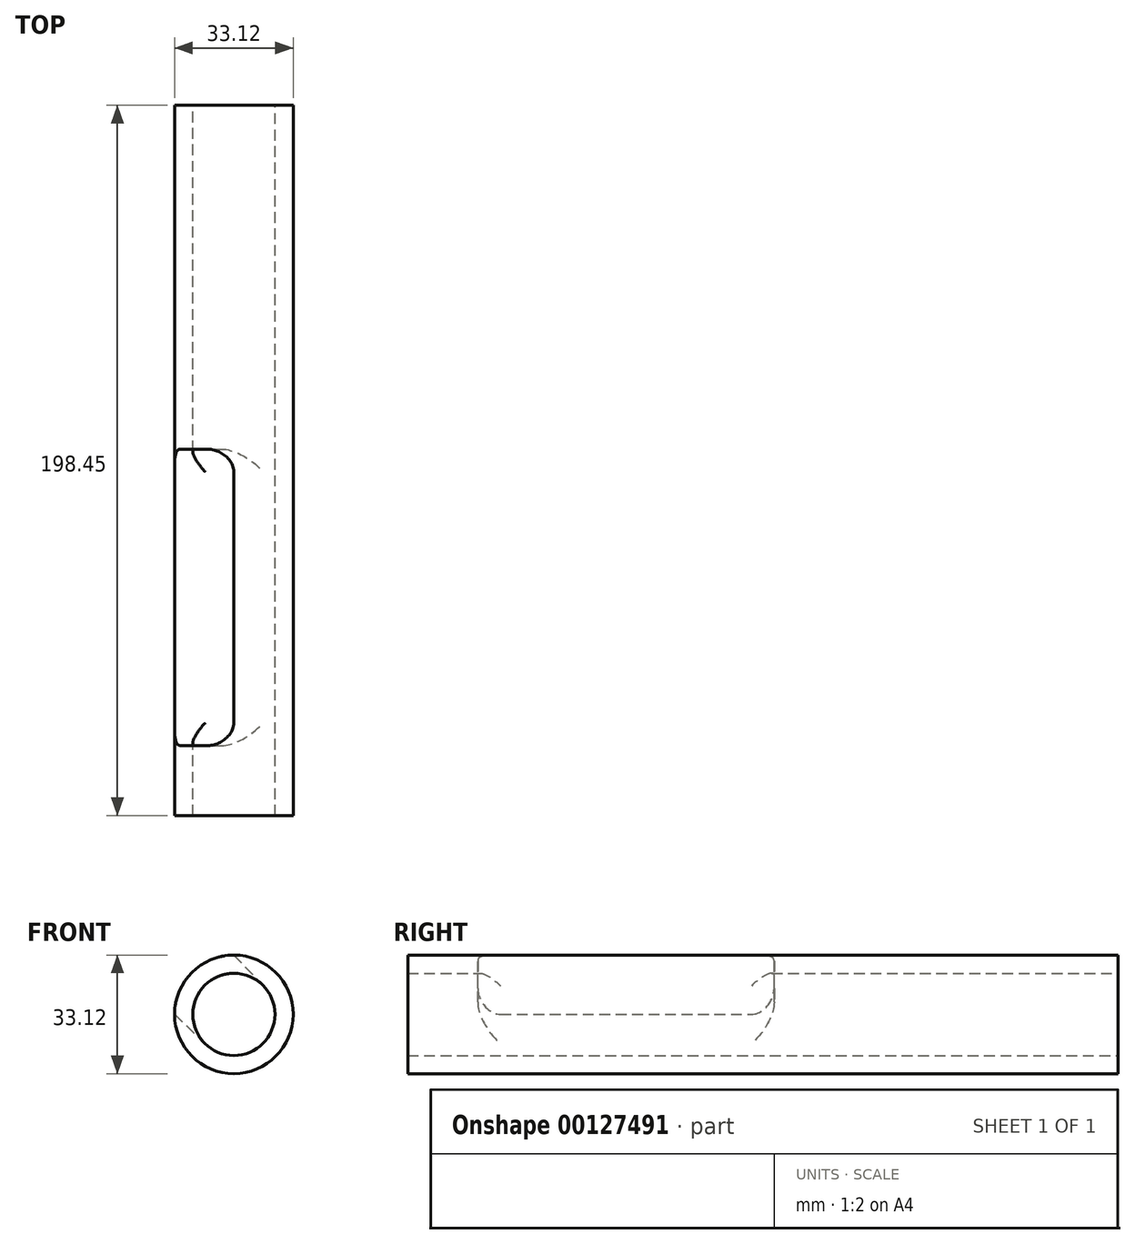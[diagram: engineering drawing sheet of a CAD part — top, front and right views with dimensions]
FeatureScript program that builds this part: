
annotation { "Feature Type Name" : "Feature", "Feature Type Description" : "" }
export const myFeature = defineFeature(function(context is Context, id is Id, definition is map)
    precondition{}
    {
        {
            var Q0;
            Q0=qCreatedBy(makeId("Front.planeOp"),FACE);
            var sketch = newSketch(context, id + "F0", { "sketchPlane" : qUnion([Q0])});
            skCircle(sketch, "E0", {"center": v(0, 0) * mm, "radius": 16.56 * mm});
            skCircle(sketch, "E1", {"center": v(0, 0) * mm, "radius": 11.48 * mm});
            skSolve(sketch);
        }
        {
            var Q0;
            Q0 = qSketchRegion(id + "F0", true);
            extrude(context, id + "F1", {"entities" : qUnion([Q0]), "depth" : 198.45 * mm});
        }
        {
            var Q0;
            Q0=makeQuery(id+"F1.opExtrude","CAP_FACE",FACE,{"disambiguationData":[OSD([sQuery(id+"F0.wireOp",EDGE,"E0"),sQuery(id+"F0.wireOp",EDGE,"E1")])],"isStart":true});
            cPlane(context, id + "F2", {"entities" : qUnion([Q0]), "cplaneType" : CPlaneType.OFFSET, "offset" : 96.1 * mm, "oppositeDirection" : true, "width" : 152.4 * mm, "height" : 152.4 * mm});
        }
        {
            var Q0;
            Q0=qCreatedBy(id+"F2.planeOp",FACE);
            var sketch = newSketch(context, id + "F3", { "sketchPlane" : qUnion([Q0])});
            skArc(sketch, "E2.0", {"start": v(16.56, 0) * mm, "mid": v(11.71, 11.71) * mm, "end": v(0, 16.56) * mm});
            skCircle(sketch, "E3.0", {"center": v(0, 0) * mm, "radius": 11.48 * mm, "construction": true});
            skLineSegment(sketch, "E4", {"start": v(0, 16.56) * mm, "end": v(-8.27, 7.96) * mm});
            skLineSegment(sketch, "E5", {"start": v(16.56, 0) * mm, "end": v(7.96, -8.27) * mm});
            skLineSegment(sketch, "E6", {"start": v(-8.27, 7.96) * mm, "end": v(7.96, -8.27) * mm});
            skSolve(sketch);
        }
        {
            var Q0;
            Q0 = qSketchRegion(id + "F3", true);
            extrude(context, id + "F4", {"entities" : qUnion([Q0]), "operationType" : NewBodyOperationType.REMOVE, "oppositeDirection" : true, "depth" : 82.8 * mm});
        }
        {
            var Q0;
            Q0=makeQuery(id+"F4.boolean.opBoolean","COPY",EDGE,{"derivedFrom":makeQuery(id+"F4.opExtrude","CAP_EDGE",EDGE,{"disambiguationData":[OSD([sQuery(id+"F3.wireOp",EDGE,"E4")])],"isStart":true})});
            var Q1;
            Q1=makeQuery(id+"F4.boolean.opBoolean","COPY",EDGE,{"derivedFrom":makeQuery(id+"F4.opExtrude","CAP_EDGE",EDGE,{"disambiguationData":[OSD([sQuery(id+"F3.wireOp",EDGE,"E5")])],"isStart":true})});
            var Q2;
            Q2=makeQuery(id+"F4.boolean.opBoolean","COPY",EDGE,{"derivedFrom":makeQuery(id+"F4.opExtrude","CAP_EDGE",EDGE,{"disambiguationData":[OSD([sQuery(id+"F3.wireOp",EDGE,"E4")])],"isStart":false})});
            var Q3;
            Q3=makeQuery(id+"F4.boolean.opBoolean","COPY",EDGE,{"derivedFrom":makeQuery(id+"F4.opExtrude","CAP_EDGE",EDGE,{"disambiguationData":[OSD([sQuery(id+"F3.wireOp",EDGE,"E5")])],"isStart":false})});
            fillet(context, id + "F5", {"entities" : qUnion([Q0, Q1, Q2, Q3]), "radius" : 6.35 * mm, "tangentPropagation" : true, "allowEdgeOverflow" : false});
        }
    });
